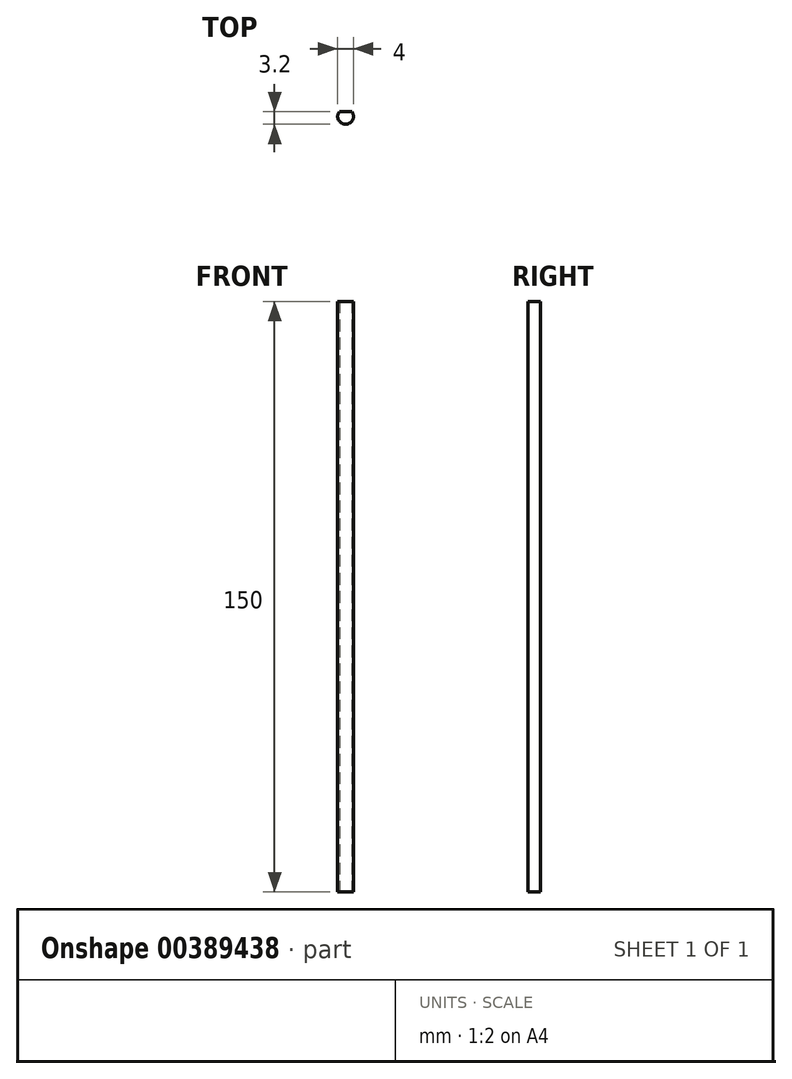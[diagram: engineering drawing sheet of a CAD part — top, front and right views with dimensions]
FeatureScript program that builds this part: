
annotation { "Feature Type Name" : "Feature", "Feature Type Description" : "" }
export const myFeature = defineFeature(function(context is Context, id is Id, definition is map)
    precondition{}
    {
        {
            var Q0;
            Q0=qCreatedBy(makeId("Top.planeOp"),FACE);
            var sketch = newSketch(context, id + "F0", { "sketchPlane" : qUnion([Q0])});
            skCircle(sketch, "E0", {"center": v(0, 0) * mm, "radius": 2 * mm});
            skLineSegment(sketch, "E1", {"start": v(1.6, 1.2) * mm, "end": v(-1.6, 1.2) * mm});
            skSolve(sketch);
        }
        {
            var Q0;
            {var subQ0=sQuery(id+"F0.wireOp",EDGE,"E1");Q0=makeQuery(id+"F0.imprint","IMPRINT",FACE,{"disambiguationData":[TD([[makeQuery(id+"F0.imprint","IMPRINT",EDGE,{"derivedFrom":subQ0}),1.0]])]});}
            extrude(context, id + "F1", {"entities" : qUnion([Q0]), "depth" : 150 * mm});
        }
    });
